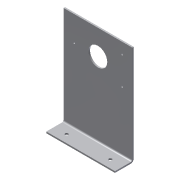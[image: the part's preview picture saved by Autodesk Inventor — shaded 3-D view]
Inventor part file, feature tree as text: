
AUTODESK INVENTOR PART (.ipt)
format: ipt  version: 2014 SP2 (Build 180246200, 246)  size: 127,488 bytes
history: native  units: in
note: dims shown in document units (in); Inventor stores cm internally (conversion verified against a paired STEP export)
features: sketch x5, sheet_metal_op x4, hole x3, other x2
ambient origin geometry x8: Origin, YZ Plane, XZ Plane, XY Plane, X Axis, Y Axis, Z Axis, Center Point
bodies: Solid1 (feature_tree)
feature tree (14):
  sheet_metal_op  "Face1"
  sheet_metal_op  "Flange1"
  hole  "Hole1"  [1 undecoded]
  hole  "Hole2"  [1 undecoded]
  hole  "Hole3"  [1 undecoded]
  sketch  "Sketch1"  dims[d0=5.5in d1=8.0in]
  other  "Plate1"
  sketch  "Sketch2"  dims[d2=0.12in d3=0.12in]
  other  "Plate2"
  sheet_metal_op  "Bend1"
  sheet_metal_op  "Corner1"
  sketch  "Sketch3"  dims[d4=0.06in d5=0.24in]
  sketch  "Sketch4"  dims[d6=0.12in]
  sketch  "Sketch5"  dims[d7=1.5in d8=90.0deg d9=0.12in d10=0.48in d11=0.12in d12=0.12in d13=0.821in d14=3.114in d16=0.828in d18=2.0in d19=0.877in d20=0.1625in d21=0.1625in d22=0.1625in d23=0.1625in d24=0.75in d25=0.375in d26=0.25in d27=0.5635in d28=0.12in d29=0.8108in d30=1.0in d31=1.0in d32=0.25in d33=0.75in d34=0.375in d35=0.25in d36=0.5635in d37=0.12in d38=0.8108in d39=4.656in d40=2.0in d41=2.75in d42=1.5in d43=0.75in d44=0.375in d45=0.25in d46=0.5635in d47=0.12in d48=0.8108in]
note: 3 required parameter values undecoded (feature->parameter linkage not recoverable at this tier; creation-order binding heuristic only, values carry confidence <= 0.55)
